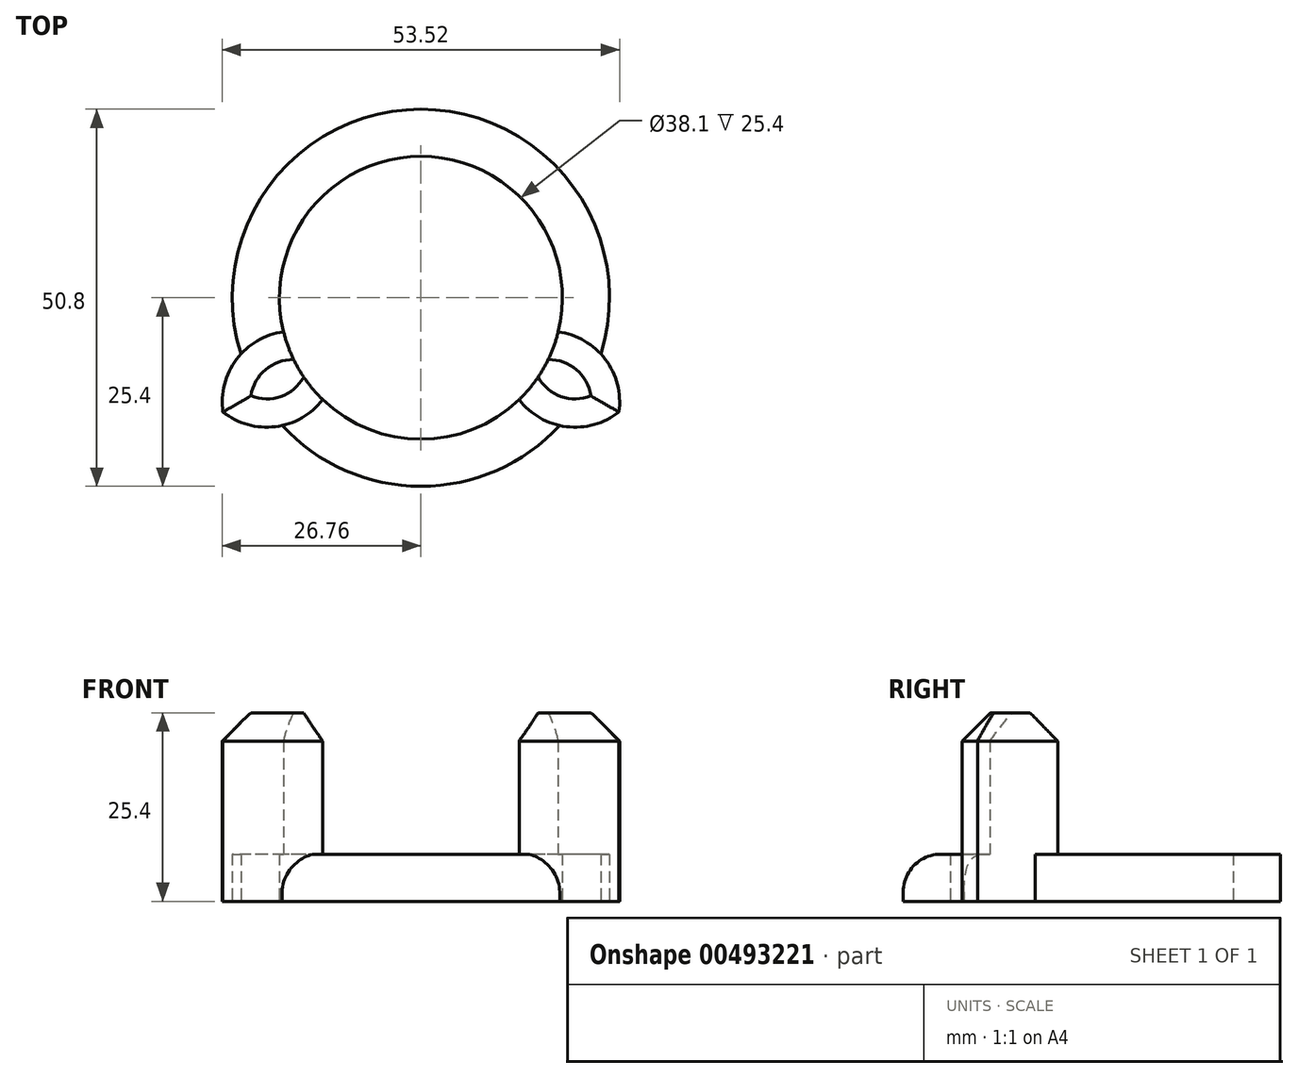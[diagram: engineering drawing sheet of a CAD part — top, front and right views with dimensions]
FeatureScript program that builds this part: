
annotation { "Feature Type Name" : "Feature", "Feature Type Description" : "" }
export const myFeature = defineFeature(function(context is Context, id is Id, definition is map)
    precondition{}
    {
        {
            var Q0;
            Q0=qCreatedBy(makeId("Top.planeOp"),FACE);
            var sketch = newSketch(context, id + "F0", { "sketchPlane" : qUnion([Q0])});
            skCircle(sketch, "E0", {"center": v(0, 0) * mm, "radius": 19.05 * mm});
            skCircle(sketch, "E1", {"center": v(0, 0) * mm, "radius": 25.4 * mm});
            skSolve(sketch);
        }
        {
            var Q0;
            Q0=makeQuery(id+"F0.imprint","IMPRINT",FACE,{"disambiguationData":[TD([[makeQuery(id+"F0.imprint","IMPRINT",EDGE,{"derivedFrom":sQuery(id+"F0.wireOp",EDGE,"E0")}),-1.0]])]});
            extrude(context, id + "F1", {"entities" : qUnion([Q0]), "depth" : 6.35 * mm});
        }
        {
            var Q0;
            Q0=makeQuery(id+"F1.opExtrude","CAP_FACE",FACE,{"disambiguationData":[OSD([sQuery(id+"F0.wireOp",EDGE,"E0"),sQuery(id+"F0.wireOp",EDGE,"E1")])],"isStart":false});
            var sketch = newSketch(context, id + "F2", { "sketchPlane" : qUnion([Q0])});
            skLineSegment(sketch, "E2", {"start": v(0, 0) * mm, "end": v(0, 36.22) * mm, "construction": true});
            skCircle(sketch, "E3", {"center": v(0, 0) * mm, "radius": 22.23 * mm, "construction": true});
            skArc(sketch, "E4.MirrorC", {"start": v(0, 30.78) * mm, "mid": v(5.24, 25.65) * mm, "end": v(5.27, 18.3) * mm});
            skCircle(sketch, "E5.0", {"center": v(0, 0) * mm, "radius": 19.05 * mm});
            skArc(sketch, "E6.trimOffspring", {"start": v(0, 30.78) * mm, "mid": v(-5.24, 25.65) * mm, "end": v(-5.27, 18.3) * mm});
            skArc(sketch, "E7.1.0", {"start": v(-26.66, -15.4) * mm, "mid": v(-19.6, -17.36) * mm, "end": v(-13.22, -13.71) * mm});
            skArc(sketch, "E7.1.1", {"start": v(-26.66, -15.4) * mm, "mid": v(-24.83, -8.29) * mm, "end": v(-18.49, -4.6) * mm});
            skArc(sketch, "E7.2.0", {"start": v(26.66, -15.4) * mm, "mid": v(24.83, -8.29) * mm, "end": v(18.49, -4.6) * mm});
            skArc(sketch, "E7.2.1", {"start": v(26.66, -15.4) * mm, "mid": v(19.6, -17.36) * mm, "end": v(13.22, -13.71) * mm});
            skSolve(sketch);
        }
        {
            var Q0;
            {var subQ0=sQuery(id+"F2.wireOp",EDGE,"E6.trimOffspring");var subQ1=sQuery(id+"F2.wireOp",EDGE,"E4.MirrorC");var subQ2=makeQuery(id+"F2.imprint","INTERSECT",VERTEX,{"derivedFrom":[subQ1,subQ0]});Q0=makeQuery(id+"F2.imprint","IMPRINT",FACE,{"disambiguationData":[TD([[makeQuery(id+"F2.imprint","IMPRINT",EDGE,{"disambiguationData":[TD([[subQ2,-1.0]])],"derivedFrom":subQ1}),-1.0]])]});}
            var Q1;
            {var subQ0=sQuery(id+"F2.wireOp",EDGE,"E5.0");var subQ1=sQuery(id+"F2.wireOp",EDGE,"E4.MirrorC");var subQ2=makeQuery(id+"F2.imprint","INTERSECT",VERTEX,{"derivedFrom":[subQ1,subQ0]});Q1=makeQuery(id+"F2.imprint","IMPRINT",FACE,{"disambiguationData":[TD([[makeQuery(id+"F2.imprint","IMPRINT",EDGE,{"disambiguationData":[TD([[subQ2,1.0]])],"derivedFrom":subQ1}),-1.0]])]});}
            var Q2;
            {var subQ0=sQuery(id+"F2.wireOp",EDGE,"E7.1.1");var subQ1=sQuery(id+"F2.wireOp",EDGE,"E7.1.0");var subQ2=makeQuery(id+"F2.imprint","INTERSECT",VERTEX,{"derivedFrom":[subQ1,subQ0]});Q2=makeQuery(id+"F2.imprint","IMPRINT",FACE,{"disambiguationData":[TD([[makeQuery(id+"F2.imprint","IMPRINT",EDGE,{"disambiguationData":[TD([[subQ2,-1.0]])],"derivedFrom":subQ1}),1.0]])]});}
            var Q3;
            {var subQ0=sQuery(id+"F2.wireOp",EDGE,"E7.1.0");var subQ1=sQuery(id+"F2.wireOp",EDGE,"E5.0");var subQ2=makeQuery(id+"F2.imprint","INTERSECT",VERTEX,{"derivedFrom":[subQ1,subQ0]});Q3=makeQuery(id+"F2.imprint","IMPRINT",FACE,{"disambiguationData":[TD([[makeQuery(id+"F2.imprint","IMPRINT",EDGE,{"disambiguationData":[TD([[subQ2,1.0]])],"derivedFrom":subQ1}),-1.0]])]});}
            var Q4;
            {var subQ0=sQuery(id+"F2.wireOp",EDGE,"E7.2.0");var subQ1=sQuery(id+"F2.wireOp",EDGE,"E5.0");var subQ2=makeQuery(id+"F2.imprint","INTERSECT",VERTEX,{"derivedFrom":[subQ1,subQ0]});Q4=makeQuery(id+"F2.imprint","IMPRINT",FACE,{"disambiguationData":[TD([[makeQuery(id+"F2.imprint","IMPRINT",EDGE,{"disambiguationData":[TD([[subQ2,1.0]])],"derivedFrom":subQ1}),-1.0]])]});}
            var Q5;
            {var subQ0=sQuery(id+"F2.wireOp",EDGE,"E7.2.1");var subQ1=sQuery(id+"F2.wireOp",EDGE,"E7.2.0");var subQ2=makeQuery(id+"F2.imprint","INTERSECT",VERTEX,{"derivedFrom":[subQ1,subQ0]});Q5=makeQuery(id+"F2.imprint","IMPRINT",FACE,{"disambiguationData":[TD([[makeQuery(id+"F2.imprint","IMPRINT",EDGE,{"disambiguationData":[TD([[subQ2,-1.0]])],"derivedFrom":subQ1}),1.0]])]});}
            extrude(context, id + "F3", {"entities" : qUnion([Q0, Q1, Q2, Q3, Q4, Q5]), "operationType" : NewBodyOperationType.ADD, "depth" : 19.05 * mm, "hasSecondDirection" : true, "secondDirectionOppositeDirection" : true, "secondDirectionDepth" : 6.35 * mm});
        }
        {
            var Q0;
            Q0=makeQuery(id+"F3.opExtrude","CAP_EDGE",EDGE,{"disambiguationData":[OSD([sQuery(id+"F2.wireOp",EDGE,"E4.MirrorC")])],"isStart":false});
            var Q1;
            Q1=makeQuery(id+"F3.opExtrude","CAP_EDGE",EDGE,{"disambiguationData":[OSD([sQuery(id+"F2.wireOp",EDGE,"E6.trimOffspring")])],"isStart":false});
            var Q2;
            Q2=makeQuery(id+"F3.opExtrude","CAP_EDGE",EDGE,{"disambiguationData":[OSD([sQuery(id+"F2.wireOp",EDGE,"E7.1.0")])],"isStart":false});
            var Q3;
            Q3=makeQuery(id+"F3.opExtrude","CAP_EDGE",EDGE,{"disambiguationData":[OSD([sQuery(id+"F2.wireOp",EDGE,"E7.1.1")])],"isStart":false});
            var Q4;
            Q4=makeQuery(id+"F3.opExtrude","CAP_EDGE",EDGE,{"disambiguationData":[OSD([sQuery(id+"F2.wireOp",EDGE,"E7.2.1")])],"isStart":false});
            var Q5;
            Q5=makeQuery(id+"F3.opExtrude","CAP_EDGE",EDGE,{"disambiguationData":[OSD([sQuery(id+"F2.wireOp",EDGE,"E7.2.0")])],"isStart":false});
            chamfer(context, id + "F4", {"entities" : qUnion([Q0, Q1, Q2, Q3, Q4, Q5]), "width" : 3.8 * mm, "tangentPropagation" : true});
        }
        {
            var Q0;
            {var subQ0=sQuery(id+"F0.wireOp",EDGE,"E1");Q0=makeQuery(id+"F3.boolean.opBoolean","SPLIT",EDGE,{"disambiguationData":[TD([makeQuery(id+"F3.opExtrude","SWEPT_FACE",FACE,{"disambiguationData":[OSD([sQuery(id+"F2.wireOp",EDGE,"E7.1.0")])]})])],"derivedFrom":makeQuery(id+"F1.opExtrude","CAP_EDGE",EDGE,{"disambiguationData":[OSD([subQ0])],"isStart":false})});}
            var Q1;
            {var subQ0=sQuery(id+"F0.wireOp",EDGE,"E1");Q1=makeQuery(id+"F3.boolean.opBoolean","SPLIT",EDGE,{"disambiguationData":[TD([makeQuery(id+"F3.opExtrude","SWEPT_FACE",FACE,{"disambiguationData":[OSD([sQuery(id+"F2.wireOp",EDGE,"E4.MirrorC")])]})])],"derivedFrom":makeQuery(id+"F1.opExtrude","CAP_EDGE",EDGE,{"disambiguationData":[OSD([subQ0])],"isStart":false})});}
            var Q2;
            {var subQ0=sQuery(id+"F0.wireOp",EDGE,"E1");Q2=makeQuery(id+"F3.boolean.opBoolean","SPLIT",EDGE,{"disambiguationData":[TD([makeQuery(id+"F3.opExtrude","SWEPT_FACE",FACE,{"disambiguationData":[OSD([sQuery(id+"F2.wireOp",EDGE,"E6.trimOffspring")])]})])],"derivedFrom":makeQuery(id+"F1.opExtrude","CAP_EDGE",EDGE,{"disambiguationData":[OSD([subQ0])],"isStart":false})});}
            fillet(context, id + "F5", {"entities" : qUnion([Q0, Q1, Q2]), "radius" : 5.08 * mm, "tangentPropagation" : true, "allowEdgeOverflow" : false});
        }
    });
